# Revit family: BS Undercounter Basin 56cm
name_source: partatom
category: Plumbing Fixtures
units: mm (PartAtom-declared; Revit-internal decimal feet)

## family parameters
Always vertical = Yes
Cut with Voids When Loaded = No
Enable Cutting in Views = No
Maintain Annotation Orientation = No
OmniClass Number = 23.45.05.14.99
OmniClass Title = Other Sanitary Washing Plumbing Fixtures
Part Type = Normal
Room Calculation Point = No
Round Connector Dimension = Use Diameter
Shared = No
Work Plane-Based = No

## types (1)
- Lecico Atlas WHB 56cm Undercounter
    Category = Basins - Undercounter
    Colour = White
    Default Elevation = 0 mm  [stored 0 ft]
    Manufacturer = Lecico SA
    Material = Vitreous China
    Model = BS Undercounter Basin 56cm
    Notes = Includes brackets
    Product Code = ATLDUOUND0560UE
    Technical Dimensions = W560 x H210 x D420mm
    URL = https://www.lecicosa.co.za
    WHB From Wall = 275 mm
    WHB Height = 600 mm
    Weight = 8.9KG

note: [stored X ft] marks values corroborated as IEEE doubles in the binary element streams (Revit-internal decimal feet)

## geometry (parser evidence)
native form markers: Sweep x3
no freeform markers — native parametric forms only
